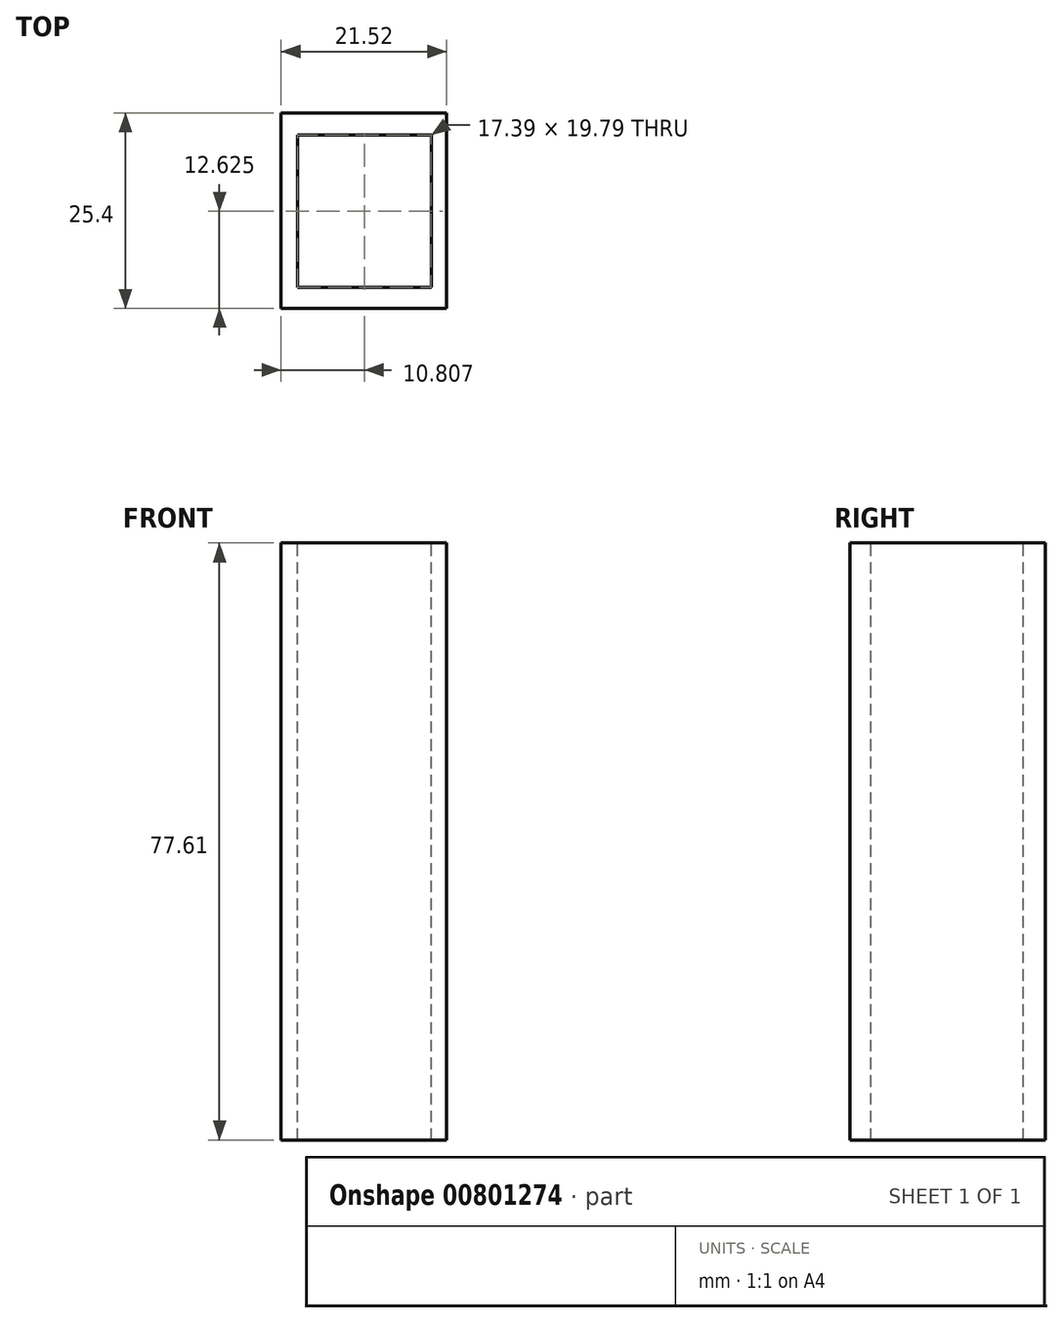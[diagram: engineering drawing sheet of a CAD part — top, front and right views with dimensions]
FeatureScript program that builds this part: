
annotation { "Feature Type Name" : "Feature", "Feature Type Description" : "" }
export const myFeature = defineFeature(function(context is Context, id is Id, definition is map)
    precondition{}
    {
        {
            var Q0;
            Q0=qCreatedBy(makeId("Front.planeOp"),FACE);
            var sketch = newSketch(context, id + "F0", { "sketchPlane" : qUnion([Q0])});
            skLineSegment(sketch, "E0.bottom", {"start": v(-19.5, 53.98) * mm, "end": v(2.02, 53.98) * mm});
            skLineSegment(sketch, "E0.top", {"start": v(-19.5, -23.63) * mm, "end": v(2.02, -23.63) * mm});
            skLineSegment(sketch, "E0.left", {"start": v(-19.5, 53.98) * mm, "end": v(-19.5, -23.63) * mm});
            skLineSegment(sketch, "E0.right", {"start": v(2.02, 53.98) * mm, "end": v(2.02, -23.63) * mm});
            skSolve(sketch);
        }
        {
            var Q0;
            Q0 = qSketchRegion(id + "F0", true);
            extrude(context, id + "F1", {"entities" : qUnion([Q0]), "depth" : 25.4 * mm, "offsetDistance" : 25.4 * mm});
        }
        {
            var Q0;
            Q0=makeQuery(id+"F1.opExtrude","SWEPT_FACE",FACE,{"disambiguationData":[OSD([sQuery(id+"F0.wireOp",EDGE,"E0.bottom")])]});
            var sketch = newSketch(context, id + "F2", { "sketchPlane" : qUnion([Q0])});
            skLineSegment(sketch, "E1", {"start": v(-17.39, -2.3) * mm, "end": v(-17.39, -22.67) * mm});
            skLineSegment(sketch, "E2", {"start": v(-17.39, -22.67) * mm, "end": v(0, -22.67) * mm});
            skLineSegment(sketch, "E3", {"start": v(0, -22.67) * mm, "end": v(0, -2.88) * mm});
            skLineSegment(sketch, "E4", {"start": v(0, -2.88) * mm, "end": v(-17.39, -2.88) * mm});
            skSolve(sketch);
        }
        {
            var Q0;
            {var subQ0=sQuery(id+"F2.wireOp",EDGE,"E2");Q0=makeQuery(id+"F2.imprint","IMPRINT",FACE,{"disambiguationData":[TD([[makeQuery(id+"F2.imprint","IMPRINT",EDGE,{"derivedFrom":subQ0}),1.0]])]});}
            extrude(context, id + "F3", {"entities" : qUnion([Q0]), "operationType" : NewBodyOperationType.REMOVE, "oppositeDirection" : true, "depth" : 152.4 * mm, "offsetDistance" : 25.4 * mm});
        }
    });
